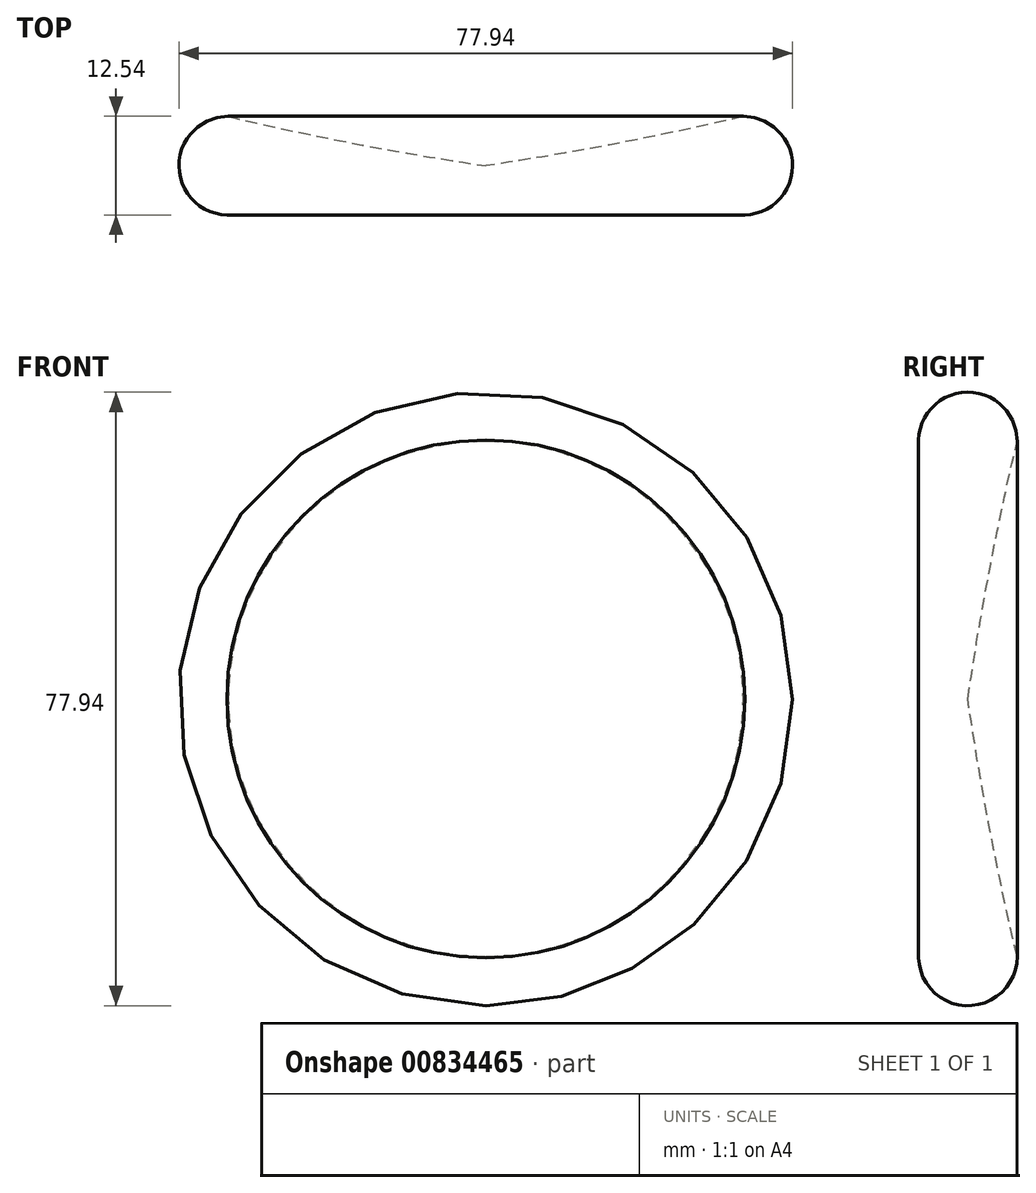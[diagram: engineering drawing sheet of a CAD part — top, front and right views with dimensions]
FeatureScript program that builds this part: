
annotation { "Feature Type Name" : "Feature", "Feature Type Description" : "" }
export const myFeature = defineFeature(function(context is Context, id is Id, definition is map)
    precondition{}
    {
        {
            var Q0;
            Q0=qCreatedBy(makeId("Top.planeOp"),FACE);
            var sketch = newSketch(context, id + "F0", { "sketchPlane" : qUnion([Q0])});
            skCircle(sketch, "E0", {"center": v(32.7, 0) * mm, "radius": 6.27 * mm});
            skLineSegment(sketch, "E1", {"start": v(32.9, -6.27) * mm, "end": v(0, -6.27) * mm});
            skLineSegment(sketch, "E2", {"start": v(0, -6.27) * mm, "end": v(0, 0) * mm});
            skArc(sketch, "E3", {"start": v(0, 0) * mm, "mid": v(16.43, 2.77) * mm, "end": v(32.73, 6.27) * mm});
            skSolve(sketch);
        }
        {
            var Q0;
            {var subQ5=sQuery(id+"F0.wireOp",EDGE,"E2");Q0=makeQuery(id+"F0.imprint","IMPRINT",FACE,{"disambiguationData":[TD([[makeQuery(id+"F0.imprint","IMPRINT",EDGE,{"derivedFrom":subQ5}),-1.0]])]});}
            var Q1;
            {var subQ0=sQuery(id+"F0.wireOp",EDGE,"E3");var subQ1=sQuery(id+"F0.wireOp",EDGE,"E0");var subQ2=makeQuery(id+"F0.imprint","INTERSECT",VERTEX,{"disambiguationData":[OD(1.0)],"derivedFrom":[subQ1,subQ0]});Q1=makeQuery(id+"F0.imprint","IMPRINT",FACE,{"disambiguationData":[TD([[makeQuery(id+"F0.imprint","IMPRINT",EDGE,{"disambiguationData":[TD([[subQ2,-1.0]])],"derivedFrom":subQ1}),1.0]])]});}
            var Q2;
            Q2=sQuery(id+"F0.wireOp",EDGE,"E2");
            revolve(context, id + "F1", {"surfaceOperationType" : NewSurfaceOperationType.NEW, "entities" : qUnion([Q0, Q1]), "axis" : qUnion([Q2]), "revolveType" : RevolveType.FULL});
        }
    });
